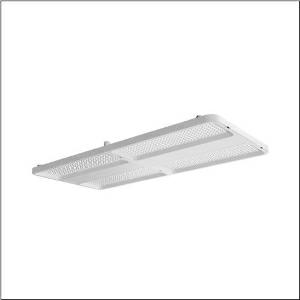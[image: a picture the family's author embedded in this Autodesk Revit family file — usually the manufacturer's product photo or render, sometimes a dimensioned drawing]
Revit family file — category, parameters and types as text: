
# Revit family: highbay_11_maxi_51hn11db4qda
name_source: partatom
category: Lighting Fixtures
units: mm (PartAtom-declared; Revit-internal decimal feet)

## family parameters
Cut with Voids When Loaded = No
Host = Face
Light Source = No
Part Type = Normal
Room Calculation Point = No
Round Connector Dimension = Use Diameter
Shared = No

## types (1)
- --- (1 x LED, 5620 lm, 27.8 W, 4000K)
    Apparent Load = 28 VA
    CIE Flux Codes = 85 97 100 100 100
    Color Rendering = 80
    Color Temperature = 4000K
    Default Elevation = 1800 mm
    Description = high bay luminaire Highbay 11 maxi; direct symmetric narrow distribution, light control with lens of PMMA; UGR ≤ 22 (X = 4H | Y = 8H | S = 0.25H | reflection values 70/50/20); luminous flux: 36.000lm; light colour: 840, colour temperature: 4000K, MacAdam ≤ 2 SDCM (initial), colour rendering: CRI > 80; luminous efficacy: 202,6lm/W; rated service life: 100.000h (L95) at AT= 25°C; control: DALI 2; luminaire connection: terminal, 5-pole, max. 2.5mm² (cable entry for one cable, Ø 8.5..16mm); mains connection: 230..240V, AC/DC 0/50..60Hz; connected load: 177,7W; protection rating (complete): IP66; insulation class (complete): insulation class I (protective earthing); protection symbol: D; impact resistance: IK08; certification: CE, ENEC, VDE, UKCA; luminaire for central battery installations according to EN 60598-2-22, internal wiring halogen-free; luminaire Suitable for use in the food industry according to the specifications of IFS-Food, HACCP and/or BRC; LABS conformity tested according to VDMA 24364:2018-05; housing frame of high-performance plastic PA6, matt traffic white (RAL 9016); cover of PMMA; dimension (LxWxH): 946 x 442 x 72mm; permissible operating ambient temperature: -40..+55°C (reducing of maximum allowable ambient temperature of 5°C with ceiling mounting); packaging unit: 1 piece; (delivery without accessories; please order mounting accessories separately)
    Height = 72 mm  [stored 0.23622 ft]
    Lamp = 1 x LED
    Lamp Light Flux = 5620 lm
    Lamp Power = 27.8 W
    Lamp count = 1
    Length = 946 mm
    Luminous efficacy = 202 lm/W
    Manufacturer = Siteco
    ModVariant = No
    Model = 51HN11DB4QDA
    Mounting Place = Ceiling
    Mounting Type = Pendant
    Number of Poles = 1
    OnlyDefault = Yes
    Power Factor = 1
    Product Name = Highbay 11 maxi
    Product group = high bay luminaire
    ProductGroupID = 902
    Protection Class = Protection class I
    Protection Degree = IP 66
    RLX_Detail_Level = 1
    RLX_Emergency_Light_Flux = 0 lm
    RLX_Emergency_Type = 0
    RLX_Emergency_Type_DB = No
    RlxData = <blob elided: 127337 chars, md5=06757536>
    Socket = socket
    Standby Power = 0 W
    System Light Flux = 5620 lm
    System Power = 28 W
    Type Comments = : DC mode (central or group accumulator) initial emergency light level
    Type Image = l_1363244.jpg
    URL = http://relux.com
    VarID = @adj_022139
    Voltage = 0 V
    Weight = 0.00 kg
    Width = 442 mm

note: [stored X ft] marks values corroborated as IEEE doubles in the binary element streams (Revit-internal decimal feet)

## geometry (parser evidence)
native form markers: Blend x4, Sweep x12
no freeform markers — native parametric forms only
